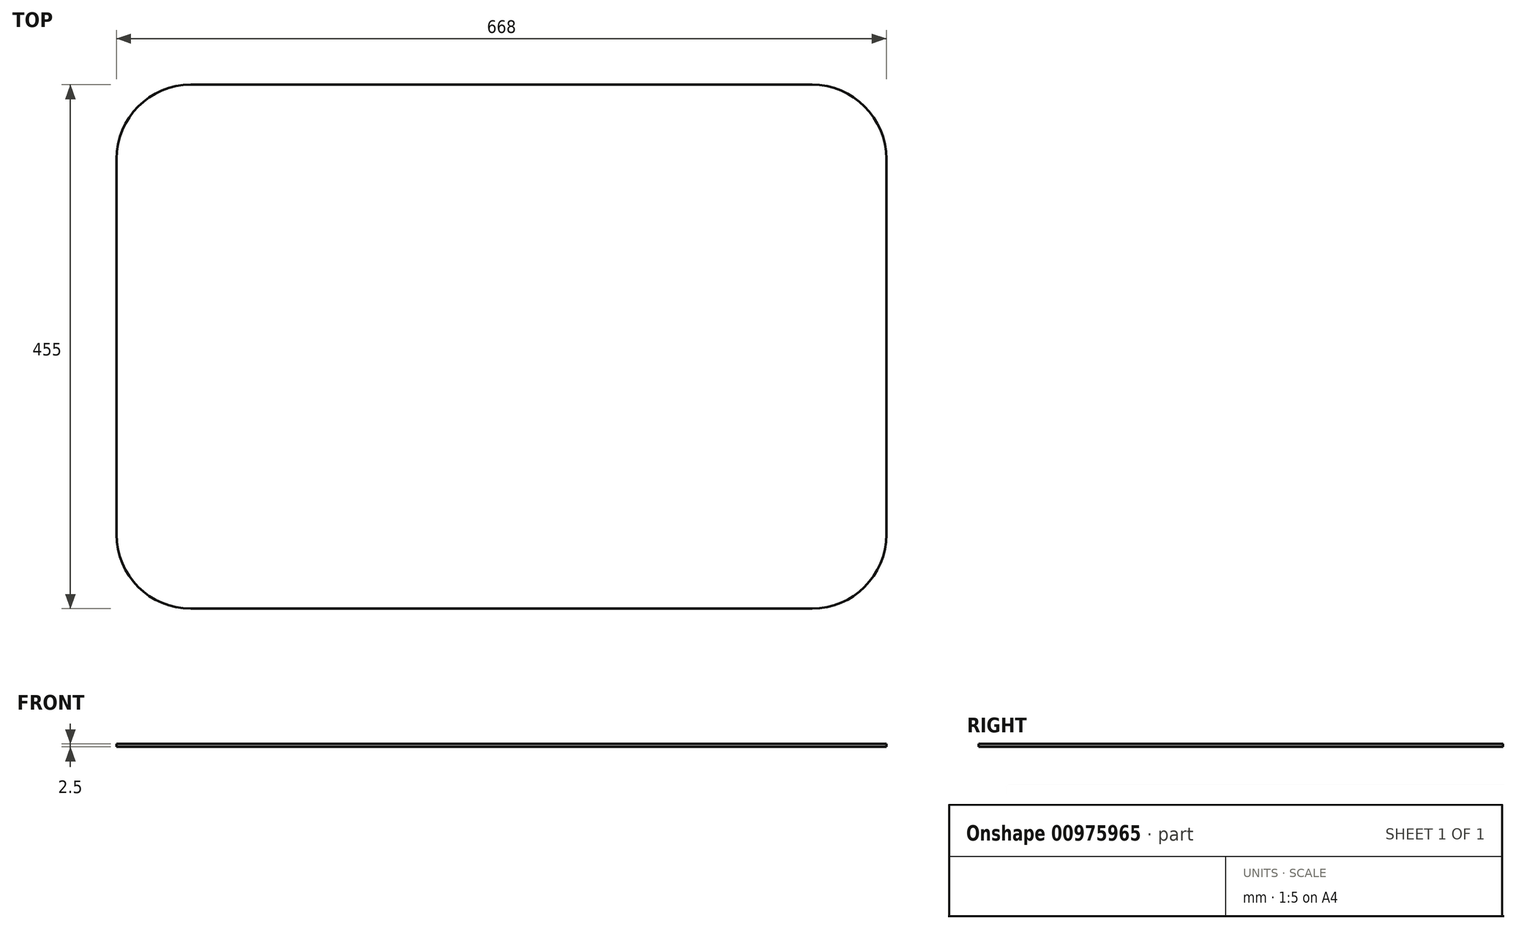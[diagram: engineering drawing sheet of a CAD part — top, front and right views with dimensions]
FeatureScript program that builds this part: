
annotation { "Feature Type Name" : "Feature", "Feature Type Description" : "" }
export const myFeature = defineFeature(function(context is Context, id is Id, definition is map)
    precondition{}
    {
        {
            var Q0;
            Q0=qCreatedBy(makeId("Top.planeOp"),FACE);
            var sketch = newSketch(context, id + "F0", { "sketchPlane" : qUnion([Q0])});
            skLineSegment(sketch, "E0.bottom", {"start": v(269.5, -227.5) * mm, "end": v(-269.5, -227.5) * mm});
            skLineSegment(sketch, "E0.top", {"start": v(269.5, 227.5) * mm, "end": v(-269.5, 227.5) * mm});
            skLineSegment(sketch, "E0.left", {"start": v(334, -163) * mm, "end": v(334, 163) * mm});
            skLineSegment(sketch, "E0.right", {"start": v(-334, -163) * mm, "end": v(-334, 163) * mm});
            skPoint(sketch, "E0.middle", {"position": v(0, 0) * mm});
            skPoint(sketch, "E1.visualSharp", {"position": v(-334, 227.5) * mm});
            skArc(sketch, "E1.filletArc", {"start": v(-269.5, 227.5) * mm, "mid": v(-315.1, 208.6) * mm, "end": v(-334, 163) * mm});
            skPoint(sketch, "E2.visualSharp", {"position": v(334, -227.5) * mm});
            skArc(sketch, "E2.filletArc", {"start": v(269.5, -227.5) * mm, "mid": v(315.1, -208.6) * mm, "end": v(334, -163) * mm});
            skPoint(sketch, "E3.visualSharp", {"position": v(334, 227.5) * mm});
            skArc(sketch, "E3.filletArc", {"start": v(334, 163) * mm, "mid": v(315.1, 208.6) * mm, "end": v(269.5, 227.5) * mm});
            skPoint(sketch, "E4.visualSharp", {"position": v(-334, -227.5) * mm});
            skArc(sketch, "E4.filletArc", {"start": v(-334, -163) * mm, "mid": v(-315.1, -208.6) * mm, "end": v(-269.5, -227.5) * mm});
            skSolve(sketch);
        }
        {
            var Q0;
            Q0 = qSketchRegion(id + "F0", true);
            extrude(context, id + "F1", {"entities" : qUnion([Q0]), "depth" : 2.5 * mm, "offsetDistance" : 25 * mm});
        }
    });
